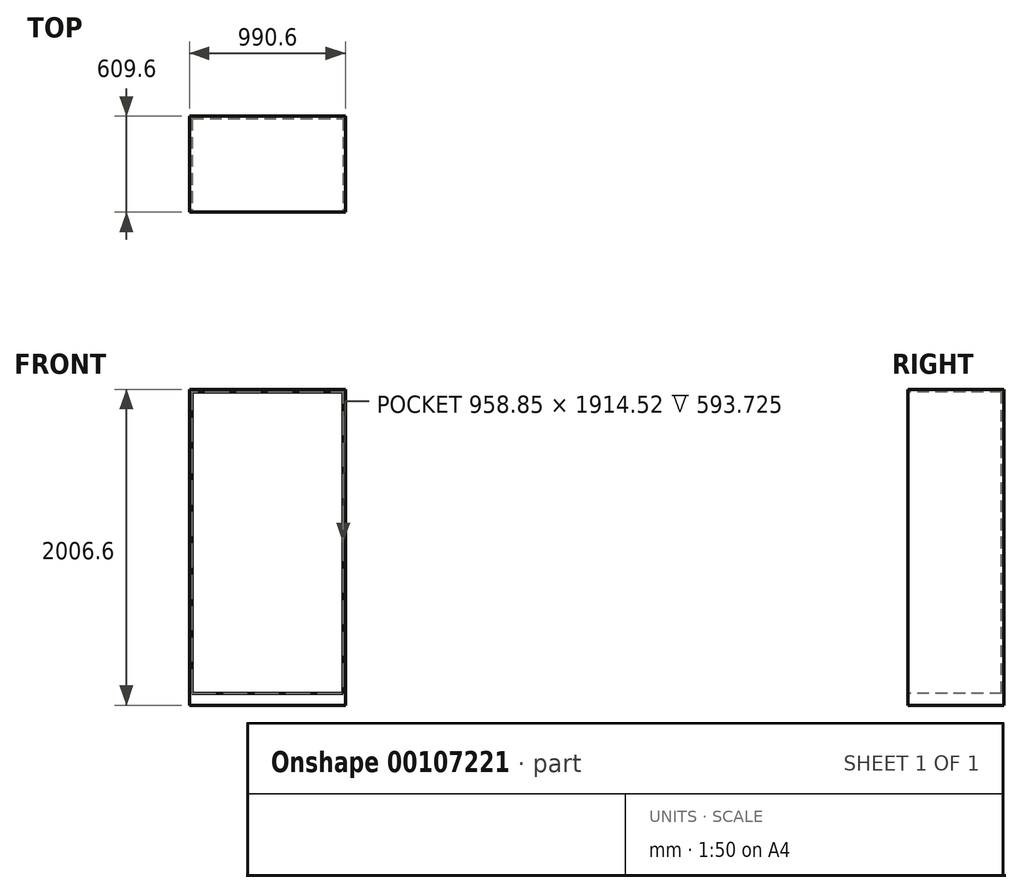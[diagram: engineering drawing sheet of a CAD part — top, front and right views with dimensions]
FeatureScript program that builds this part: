
annotation { "Feature Type Name" : "Feature", "Feature Type Description" : "" }
export const myFeature = defineFeature(function(context is Context, id is Id, definition is map)
    precondition{}
    {
        {
            var Q0;
            Q0=qCreatedBy(makeId("Front.planeOp"),FACE);
            var sketch = newSketch(context, id + "F0", { "sketchPlane" : qUnion([Q0])});
            skLineSegment(sketch, "E0.bottom", {"start": v(-495.3, 0) * mm, "end": v(495.3, 0) * mm});
            skLineSegment(sketch, "E0.top", {"start": v(-495.3, 2006.6) * mm, "end": v(495.3, 2006.6) * mm});
            skLineSegment(sketch, "E0.left", {"start": v(-495.3, 0) * mm, "end": v(-495.3, 2006.6) * mm});
            skLineSegment(sketch, "E0.right", {"start": v(495.3, 0) * mm, "end": v(495.3, 2006.6) * mm});
            skSolve(sketch);
        }
        {
            var Q0;
            Q0=makeQuery(id+"F0.imprint","IMPRINT",FACE,{"disambiguationData":[TD([[makeQuery(id+"F0.imprint","IMPRINT",EDGE,{"derivedFrom":sQuery(id+"F0.wireOp",EDGE,"E0.bottom")}),1.0]])]});
            extrude(context, id + "F1", {"entities" : qUnion([Q0]), "depth" : 609.6 * mm});
        }
        {
            var Q0;
            Q0=makeQuery(id+"F1.opExtrude","CAP_FACE",FACE,{"disambiguationData":[OSD([sQuery(id+"F0.wireOp",EDGE,"E0.bottom"),sQuery(id+"F0.wireOp",EDGE,"E0.top"),sQuery(id+"F0.wireOp",EDGE,"E0.left"),sQuery(id+"F0.wireOp",EDGE,"E0.right")])],"isStart":false});
            var sketch = newSketch(context, id + "F2", { "sketchPlane" : qUnion([Q0])});
            skLineSegment(sketch, "E1.bottom", {"start": v(-479.42, 76.2) * mm, "end": v(479.42, 76.2) * mm});
            skLineSegment(sketch, "E1.top", {"start": v(-479.43, 1990.73) * mm, "end": v(479.43, 1990.73) * mm});
            skLineSegment(sketch, "E1.left", {"start": v(-479.43, 76.2) * mm, "end": v(-479.43, 1990.72) * mm});
            skLineSegment(sketch, "E1.right", {"start": v(479.42, 76.2) * mm, "end": v(479.42, 1990.73) * mm});
            skLineSegment(sketch, "E2", {"start": v(0, 76.2) * mm, "end": v(0, 0) * mm, "construction": true});
            skSolve(sketch);
        }
        {
            var Q0;
            Q0 = qSketchRegion(id + "F2", true);
            extrude(context, id + "F3", {"entities" : qUnion([Q0]), "operationType" : NewBodyOperationType.REMOVE, "oppositeDirection" : true, "depth" : 593.73 * mm});
        }
    });
